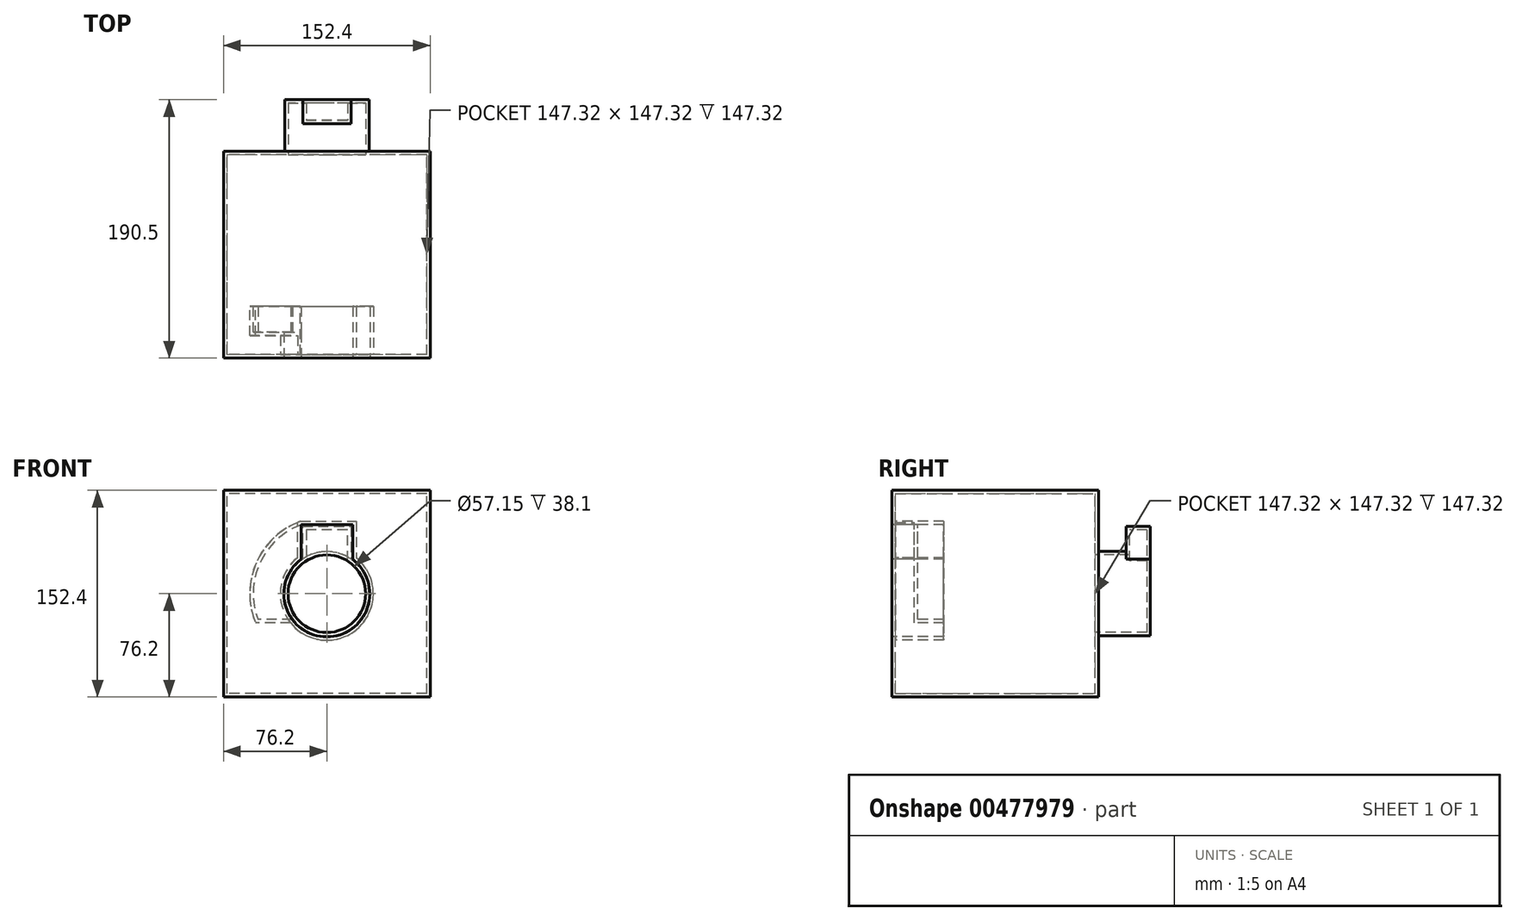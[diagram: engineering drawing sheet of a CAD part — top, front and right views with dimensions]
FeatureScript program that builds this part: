
annotation { "Feature Type Name" : "Feature", "Feature Type Description" : "" }
export const myFeature = defineFeature(function(context is Context, id is Id, definition is map)
    precondition{}
    {
        {
            var Q0;
            Q0=qCreatedBy(makeId("Front.planeOp"),FACE);
            var sketch = newSketch(context, id + "F0", { "sketchPlane" : qUnion([Q0])});
            skLineSegment(sketch, "E0.bottom", {"start": v(76.2, -76.2) * mm, "end": v(-76.2, -76.2) * mm});
            skLineSegment(sketch, "E0.top", {"start": v(76.2, 76.2) * mm, "end": v(-76.2, 76.2) * mm});
            skLineSegment(sketch, "E0.left", {"start": v(76.2, -76.2) * mm, "end": v(76.2, 76.2) * mm});
            skLineSegment(sketch, "E0.right", {"start": v(-76.2, -76.2) * mm, "end": v(-76.2, 76.2) * mm});
            skPoint(sketch, "E0.middle", {"position": v(0, 0) * mm});
            skSolve(sketch);
        }
        {
            var Q0;
            Q0=makeQuery(id+"F0.imprint","IMPRINT",FACE,{"disambiguationData":[TD([[makeQuery(id+"F0.imprint","IMPRINT",EDGE,{"derivedFrom":sQuery(id+"F0.wireOp",EDGE,"E0.bottom")}),-1.0]])]});
            extrude(context, id + "F1", {"entities" : qUnion([Q0]), "depth" : 152.4 * mm});
        }
        {
            var Q0;
            Q0=makeQuery(id+"F1.opExtrude","CAP_FACE",FACE,{"disambiguationData":[OSD([sQuery(id+"F0.wireOp",EDGE,"E0.bottom"),sQuery(id+"F0.wireOp",EDGE,"E0.top"),sQuery(id+"F0.wireOp",EDGE,"E0.left"),sQuery(id+"F0.wireOp",EDGE,"E0.right")])],"isStart":false});
            var sketch = newSketch(context, id + "F2", { "sketchPlane" : qUnion([Q0])});
            skArc(sketch, "E1", {"start": v(-19.05, 25.4) * mm, "mid": v(0, -31.75) * mm, "end": v(19.05, 25.4) * mm});
            skLineSegment(sketch, "E2", {"start": v(-19.05, 25.4) * mm, "end": v(-19.05, 50.8) * mm});
            skLineSegment(sketch, "E3", {"start": v(-19.05, 50.8) * mm, "end": v(19.05, 50.8) * mm});
            skLineSegment(sketch, "E4", {"start": v(19.05, 50.8) * mm, "end": v(19.05, 25.4) * mm});
            skSolve(sketch);
        }
        {
            var Q0;
            Q0=makeQuery(id+"F2.imprint","IMPRINT",FACE,{"disambiguationData":[TD([[makeQuery(id+"F2.imprint","IMPRINT",EDGE,{"derivedFrom":sQuery(id+"F2.wireOp",EDGE,"E1")}),1.0]])]});
            extrude(context, id + "F3", {"entities" : qUnion([Q0]), "operationType" : NewBodyOperationType.REMOVE, "oppositeDirection" : true, "depth" : 38.1 * mm});
        }
        {
            var Q0;
            Q0=makeQuery(id+"F3.boolean.opBoolean","COPY",FACE,{"derivedFrom":makeQuery(id+"F3.opExtrude","SWEPT_FACE",FACE,{"disambiguationData":[OSD([sQuery(id+"F2.wireOp",EDGE,"E2")])]})});
            var sketch = newSketch(context, id + "F4", { "sketchPlane" : qUnion([Q0])});
            skLineSegment(sketch, "E5", {"start": v(-133.35, 25.4) * mm, "end": v(-133.35, 50.8) * mm});
            skLineSegment(sketch, "E6", {"start": v(-133.35, 50.8) * mm, "end": v(-114.3, 50.8) * mm});
            skLineSegment(sketch, "E7", {"start": v(-114.3, 50.8) * mm, "end": v(-114.3, 25.4) * mm});
            skLineSegment(sketch, "E8", {"start": v(-114.3, 25.4) * mm, "end": v(-133.35, 25.4) * mm});
            skSolve(sketch);
        }
        {
            var Q0;
            Q0=makeQuery(id+"F4.imprint","IMPRINT",FACE,{"disambiguationData":[TD([[makeQuery(id+"F4.imprint","IMPRINT",EDGE,{"derivedFrom":sQuery(id+"F4.wireOp",EDGE,"E5")}),-1.0]])]});
            var Q1;
            Q1=makeQuery(id+"F3.boolean.opBoolean","COPY",FACE,{"derivedFrom":makeQuery(id+"F3.opExtrude","SWEPT_FACE",FACE,{"disambiguationData":[OSD([sQuery(id+"F2.wireOp",EDGE,"E1")])]})});
            revolve(context, id + "F5", {"operationType" : NewBodyOperationType.REMOVE, "entities" : qUnion([Q0]), "axis" : qUnion([Q1]), "revolveType" : RevolveType.ONE_DIRECTION, "oppositeDirection" : true, "angle" : 90 * degree});
        }
        {
            var Q0;
            Q0=makeQuery(id+"F1.opExtrude","CAP_FACE",FACE,{"disambiguationData":[OSD([sQuery(id+"F0.wireOp",EDGE,"E0.bottom"),sQuery(id+"F0.wireOp",EDGE,"E0.top"),sQuery(id+"F0.wireOp",EDGE,"E0.left"),sQuery(id+"F0.wireOp",EDGE,"E0.right")])],"isStart":true});
            var sketch = newSketch(context, id + "F6", { "sketchPlane" : qUnion([Q0])});
            skArc(sketch, "E9", {"start": v(-17.78, 25.53) * mm, "mid": v(0, -31.12) * mm, "end": v(17.78, 25.53) * mm});
            skLineSegment(sketch, "E10", {"start": v(-17.78, 25.53) * mm, "end": v(-17.78, 49.66) * mm});
            skLineSegment(sketch, "E11", {"start": v(-17.78, 49.66) * mm, "end": v(17.78, 49.66) * mm});
            skLineSegment(sketch, "E12", {"start": v(17.78, 49.66) * mm, "end": v(17.78, 25.53) * mm});
            skSolve(sketch);
        }
        {
            var Q0;
            Q0=makeQuery(id+"F6.imprint","IMPRINT",FACE,{"disambiguationData":[TD([[makeQuery(id+"F6.imprint","IMPRINT",EDGE,{"derivedFrom":sQuery(id+"F6.wireOp",EDGE,"E9")}),1.0]])]});
            extrude(context, id + "F7", {"entities" : qUnion([Q0]), "operationType" : NewBodyOperationType.ADD, "depth" : 38.1 * mm});
        }
        {
            var Q0;
            Q0=makeQuery(id+"F7.opExtrude","SWEPT_FACE",FACE,{"disambiguationData":[OSD([sQuery(id+"F6.wireOp",EDGE,"E12")])]});
            var sketch = newSketch(context, id + "F8", { "sketchPlane" : qUnion([Q0])});
            skLineSegment(sketch, "E13", {"start": v(-20.32, 25.53) * mm, "end": v(0, 25.53) * mm});
            skLineSegment(sketch, "E14", {"start": v(0, 49.66) * mm, "end": v(-20.32, 49.66) * mm});
            skPoint(sketch, "E15.start.orphan", {"position": v(-22.4, 25.53) * mm});
            skLineSegment(sketch, "E16", {"start": v(-20.32, 25.53) * mm, "end": v(-20.32, 49.66) * mm});
            skLineSegment(sketch, "E17", {"start": v(0, 49.66) * mm, "end": v(0, 25.53) * mm});
            skSolve(sketch);
        }
        {
            var Q0;
            Q0=makeQuery(id+"F8.imprint","IMPRINT",FACE,{"disambiguationData":[TD([[makeQuery(id+"F8.imprint","IMPRINT",EDGE,{"derivedFrom":sQuery(id+"F8.wireOp",EDGE,"E13")}),1.0]])]});
            var Q1;
            Q1=makeQuery(id+"F7.opExtrude","SWEPT_FACE",FACE,{"disambiguationData":[OSD([sQuery(id+"F6.wireOp",EDGE,"E9")])]});
            revolve(context, id + "F9", {"operationType" : NewBodyOperationType.REMOVE, "entities" : qUnion([Q0]), "axis" : qUnion([Q1]), "revolveType" : RevolveType.ONE_DIRECTION, "oppositeDirection" : true, "angle" : 90 * degree});
        }
        {
            var Q0;
            Q0=makeQuery(id+"F5.boolean.opBoolean","MERGE",FACE,{"derivedFrom":[makeQuery(id+"F3.boolean.opBoolean","COPY",FACE,{"derivedFrom":makeQuery(id+"F3.opExtrude","CAP_FACE",FACE,{"disambiguationData":[OSD([sQuery(id+"F2.wireOp",EDGE,"E1"),sQuery(id+"F2.wireOp",EDGE,"E2"),sQuery(id+"F2.wireOp",EDGE,"E3"),sQuery(id+"F2.wireOp",EDGE,"E4")])],"isStart":false})}),makeQuery(id+"F5.opRevolve","SWEPT_FACE",FACE,{"disambiguationData":[OSD([sQuery(id+"F4.wireOp",EDGE,"E7")])]})]});
            shell(context, id + "F10", {"entities" : qUnion([Q0]), "thickness" : 2.54 * mm});
        }
    });
